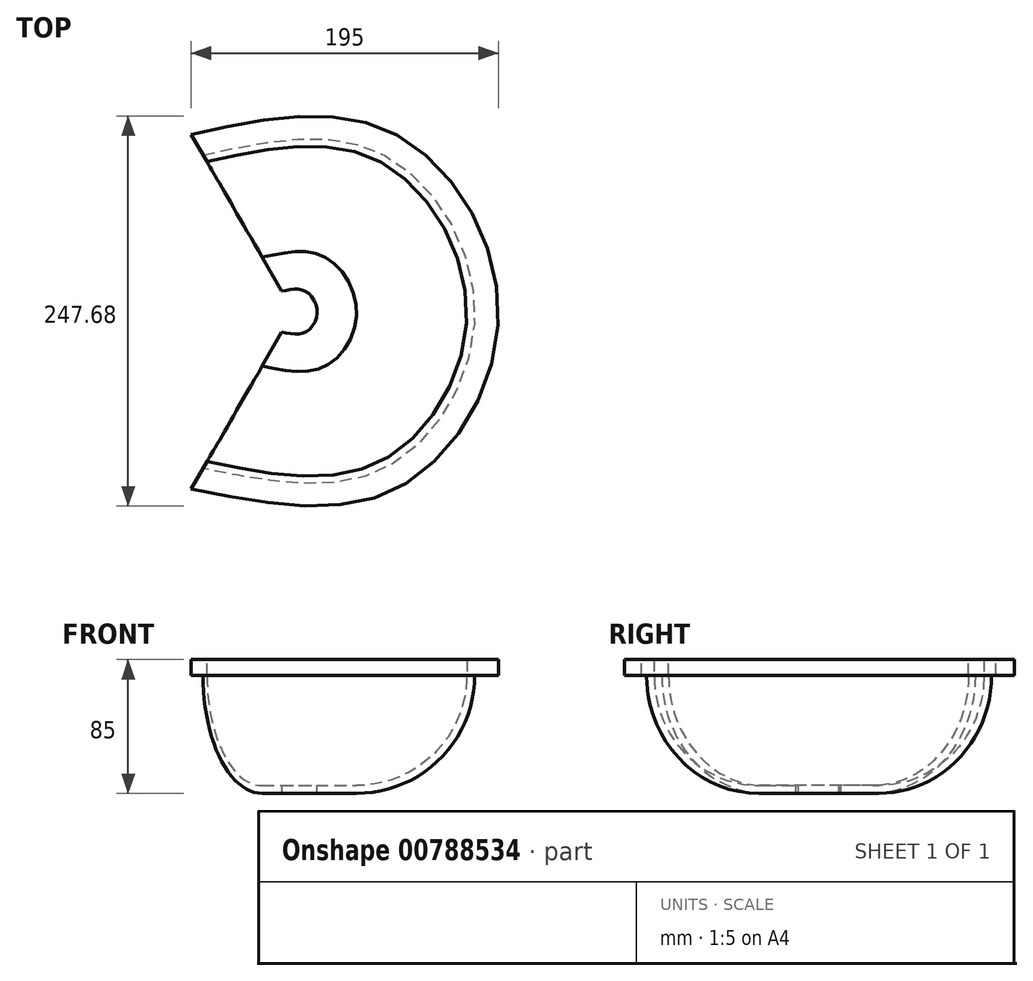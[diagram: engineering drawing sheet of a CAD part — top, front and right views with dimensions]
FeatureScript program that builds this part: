
annotation { "Feature Type Name" : "Feature", "Feature Type Description" : "" }
export const myFeature = defineFeature(function(context is Context, id is Id, definition is map)
    precondition{}
    {
        {
            var Q0;
            Q0=qCreatedBy(makeId("Front.planeOp"),FACE);
            var sketch = newSketch(context, id + "F0", { "sketchPlane" : qUnion([Q0])});
            skLineSegment(sketch, "E0.bottom", {"start": v(40, 0) * mm, "end": v(15, 0) * mm});
            skLineSegment(sketch, "E0.top", {"start": v(40, 5) * mm, "end": v(15, 5) * mm});
            skLineSegment(sketch, "E0.left", {"start": v(40, 0) * mm, "end": v(40, 5) * mm, "construction": true});
            skLineSegment(sketch, "E0.right", {"start": v(15, 0) * mm, "end": v(15, 5) * mm});
            skPoint(sketch, "E0.middle", {"position": v(27.5, 2.5) * mm});
            skLineSegment(sketch, "E1.top", {"start": v(130, 85) * mm, "end": v(110, 85) * mm});
            skLineSegment(sketch, "E1.left", {"start": v(130, 75) * mm, "end": v(130, 85) * mm});
            skLineSegment(sketch, "E1.right", {"start": v(110, 75) * mm, "end": v(110, 85) * mm});
            skArc(sketch, "E2", {"start": v(40, 0) * mm, "mid": v(93.03, 21.97) * mm, "end": v(115, 75) * mm});
            skArc(sketch, "E3", {"start": v(40, 5) * mm, "mid": v(89.5, 25.5) * mm, "end": v(110, 75) * mm});
            skLineSegment(sketch, "E4", {"start": v(130, 75) * mm, "end": v(115, 75) * mm});
            skLineSegment(sketch, "E5", {"start": v(0, 0) * mm, "end": v(0, 50) * mm, "construction": true});
            skLineSegment(sketch, "E6", {"start": v(-65.77, 0) * mm, "end": v(133.27, 0) * mm, "construction": true});
            skSolve(sketch);
        }
        {
            var Q0;
            Q0=sQuery(id+"F0.wireOp",EDGE,"E5");
            cPlane(context, id + "F1", {"entities" : qUnion([Q0]), "cplaneType" : CPlaneType.LINE_ANGLE, "offset" : 25 * mm, "angle" : 30 * degree, "oppositeDirection" : true, "width" : 150 * mm, "height" : 150 * mm});
        }
        {
            var Q0;
            Q0=qCreatedBy(id+"F1.planeOp",FACE);
            var sketch = newSketch(context, id + "F2", { "sketchPlane" : qUnion([Q0])});
            skLineSegment(sketch, "E7.bottom", {"start": v(40, 0) * mm, "end": v(15, 0) * mm});
            skLineSegment(sketch, "E7.top", {"start": v(40, 5) * mm, "end": v(15, 5) * mm});
            skLineSegment(sketch, "E7.left", {"start": v(40, 0) * mm, "end": v(40, 5) * mm, "construction": true});
            skLineSegment(sketch, "E7.right", {"start": v(15, 0) * mm, "end": v(15, 5) * mm});
            skPoint(sketch, "E7.middle", {"position": v(27.5, 2.5) * mm});
            skLineSegment(sketch, "E8.top", {"start": v(130, 85) * mm, "end": v(110, 85) * mm});
            skLineSegment(sketch, "E8.left", {"start": v(130, 75) * mm, "end": v(130, 85) * mm});
            skLineSegment(sketch, "E8.right", {"start": v(110, 75) * mm, "end": v(110, 85) * mm});
            skArc(sketch, "E9", {"start": v(40, 0) * mm, "mid": v(93.03, 21.97) * mm, "end": v(115, 75) * mm});
            skArc(sketch, "E10", {"start": v(40, 5) * mm, "mid": v(89.5, 25.5) * mm, "end": v(110, 75) * mm});
            skLineSegment(sketch, "E11", {"start": v(130, 75) * mm, "end": v(115, 75) * mm});
            skLineSegment(sketch, "E12", {"start": v(0, 0) * mm, "end": v(0, 50) * mm, "construction": true});
            skLineSegment(sketch, "E13", {"start": v(-129.3, 0) * mm, "end": v(69.73, 0) * mm, "construction": true});
            skLineSegment(sketch, "E14.MirrorCS", {"start": v(-40, 5) * mm, "end": v(-15, 5) * mm});
            skLineSegment(sketch, "E15.MirrorCS", {"start": v(-110, 75) * mm, "end": v(-110, 85) * mm});
            skLineSegment(sketch, "E16.MirrorCS", {"start": v(-130, 75) * mm, "end": v(-115, 75) * mm});
            skLineSegment(sketch, "E17.MirrorCS", {"start": v(-130, 85) * mm, "end": v(-110, 85) * mm});
            skLineSegment(sketch, "E18.MirrorCS", {"start": v(-130, 75) * mm, "end": v(-130, 85) * mm});
            skArc(sketch, "E19.MirrorCS", {"start": v(-40, 5) * mm, "mid": v(-89.5, 25.5) * mm, "end": v(-110, 75) * mm});
            skArc(sketch, "E20.MirrorCS", {"start": v(-40, 0) * mm, "mid": v(-93.03, 21.97) * mm, "end": v(-115, 75) * mm});
            skLineSegment(sketch, "E21", {"start": v(-40, 0) * mm, "end": v(-15, 0) * mm});
            skLineSegment(sketch, "E22", {"start": v(-15, 5) * mm, "end": v(-15, 0) * mm});
            skSolve(sketch);
        }
        {
            var Q0;
            Q0=sQuery(id+"F0.wireOp",EDGE,"E5");
            cPlane(context, id + "F3", {"entities" : qUnion([Q0]), "cplaneType" : CPlaneType.LINE_ANGLE, "offset" : 25 * mm, "angle" : 150 * degree, "oppositeDirection" : true, "width" : 150 * mm, "height" : 150 * mm});
        }
        {
            var Q0;
            Q0=qCreatedBy(id+"F3.planeOp",FACE);
            var sketch = newSketch(context, id + "F4", { "sketchPlane" : qUnion([Q0])});
            skLineSegment(sketch, "E23.bottom", {"start": v(40, 0) * mm, "end": v(15, 0) * mm});
            skLineSegment(sketch, "E23.top", {"start": v(40, 5) * mm, "end": v(15, 5) * mm});
            skLineSegment(sketch, "E23.left", {"start": v(40, 0) * mm, "end": v(40, 5) * mm, "construction": true});
            skLineSegment(sketch, "E23.right", {"start": v(15, 0) * mm, "end": v(15, 5) * mm});
            skPoint(sketch, "E23.middle", {"position": v(27.5, 2.5) * mm});
            skLineSegment(sketch, "E24.top", {"start": v(130, 85) * mm, "end": v(110, 85) * mm});
            skLineSegment(sketch, "E24.left", {"start": v(130, 75) * mm, "end": v(130, 85) * mm});
            skLineSegment(sketch, "E24.right", {"start": v(110, 75) * mm, "end": v(110, 85) * mm});
            skArc(sketch, "E25", {"start": v(40, 0) * mm, "mid": v(93.03, 21.97) * mm, "end": v(115, 75) * mm});
            skArc(sketch, "E26", {"start": v(40, 5) * mm, "mid": v(89.5, 25.5) * mm, "end": v(110, 75) * mm});
            skLineSegment(sketch, "E27", {"start": v(130, 75) * mm, "end": v(115, 75) * mm});
            skLineSegment(sketch, "E28", {"start": v(0, 0) * mm, "end": v(0, 50) * mm, "construction": true});
            skLineSegment(sketch, "E29", {"start": v(-129.3, 0) * mm, "end": v(69.73, 0) * mm, "construction": true});
            skLineSegment(sketch, "E30.MirrorCS", {"start": v(-110, 75) * mm, "end": v(-110, 85) * mm});
            skLineSegment(sketch, "E31.MirrorCS", {"start": v(-130, 85) * mm, "end": v(-110, 85) * mm});
            skLineSegment(sketch, "E32.MirrorCS", {"start": v(-130, 75) * mm, "end": v(-130, 85) * mm});
            skLineSegment(sketch, "E33.MirrorCS", {"start": v(129.3, 0) * mm, "end": v(-69.73, 0) * mm, "construction": true});
            skLineSegment(sketch, "E34.MirrorCS", {"start": v(-40, 0) * mm, "end": v(-40, 5) * mm, "construction": true});
            skLineSegment(sketch, "E35.MirrorCS", {"start": v(-15, 0) * mm, "end": v(-15, 5) * mm});
            skLineSegment(sketch, "E36.MirrorCS", {"start": v(-40, 0) * mm, "end": v(-15, 0) * mm});
            skArc(sketch, "E37.MirrorCS", {"start": v(-40, 5) * mm, "mid": v(-89.5, 25.5) * mm, "end": v(-110, 75) * mm});
            skArc(sketch, "E38.MirrorCS", {"start": v(-40, 0) * mm, "mid": v(-93.03, 21.97) * mm, "end": v(-115, 75) * mm});
            skLineSegment(sketch, "E39.MirrorCS", {"start": v(-40, 5) * mm, "end": v(-15, 5) * mm});
            skLineSegment(sketch, "E40", {"start": v(-115, 75) * mm, "end": v(-130, 75) * mm});
            skLineSegment(sketch, "E41", {"start": v(-15, 0) * mm, "end": v(0, 0) * mm, "construction": true});
            skSolve(sketch);
        }
        {
            var Q0;
            Q0=makeQuery(id+"F4.imprint","IMPRINT",FACE,{"disambiguationData":[TD([[makeQuery(id+"F4.imprint","IMPRINT",EDGE,{"derivedFrom":sQuery(id+"F4.wireOp",EDGE,"E30.MirrorCS")}),1.0]])]});
            var Q1;
            Q1=makeQuery(id+"F2.imprint","IMPRINT",FACE,{"disambiguationData":[TD([[makeQuery(id+"F2.imprint","IMPRINT",EDGE,{"derivedFrom":sQuery(id+"F2.wireOp",EDGE,"E7.bottom")}),-1.0]])]});
            var Q2;
            Q2=makeQuery(id+"F0.imprint","IMPRINT",FACE,{"disambiguationData":[TD([[makeQuery(id+"F0.imprint","IMPRINT",EDGE,{"derivedFrom":sQuery(id+"F0.wireOp",EDGE,"E0.bottom")}),-1.0]])]});
            var Q3;
            Q3=makeQuery(id+"F4.imprint","IMPRINT",FACE,{"disambiguationData":[TD([[makeQuery(id+"F4.imprint","IMPRINT",EDGE,{"derivedFrom":sQuery(id+"F4.wireOp",EDGE,"E23.bottom")}),-1.0]])]});
            var Q4;
            Q4=makeQuery(id+"F2.imprint","IMPRINT",FACE,{"disambiguationData":[TD([[makeQuery(id+"F2.imprint","IMPRINT",EDGE,{"derivedFrom":sQuery(id+"F2.wireOp",EDGE,"E14.MirrorCS")}),-1.0]])]});
            loft(context, id + "F5", {"sheetProfilesArray" : [{ "sheetProfileEntities" : qUnion([Q0]) }, { "sheetProfileEntities" : qUnion([Q1]) }, { "sheetProfileEntities" : qUnion([Q2]) }, { "sheetProfileEntities" : qUnion([Q3]) }, { "sheetProfileEntities" : qUnion([Q4]) }]});
        }
    });
